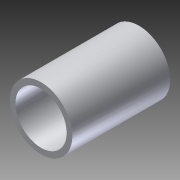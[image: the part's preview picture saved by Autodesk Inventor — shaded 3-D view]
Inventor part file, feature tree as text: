
AUTODESK INVENTOR PART (.ipt)
format: ipt  version: 2014 SP1 (Build 180222100, 222)  size: 86,528 bytes
history: native  units: in
note: dims shown in document units (in); Inventor stores cm internally (conversion verified against a paired STEP export)
features: extrude x1, sketch x1
ambient origin geometry x8: Origin, YZ Plane, XZ Plane, XY Plane, X Axis, Y Axis, Z Axis, Center Point
bodies: Solid1 (feature_tree)
feature tree (2):
  extrude  "Extrusion1"  Depth=2.6in
  sketch  "Sketch1"  dims[d0=1.36in d1=1.66in d2=2.6in d3=0.0in]
